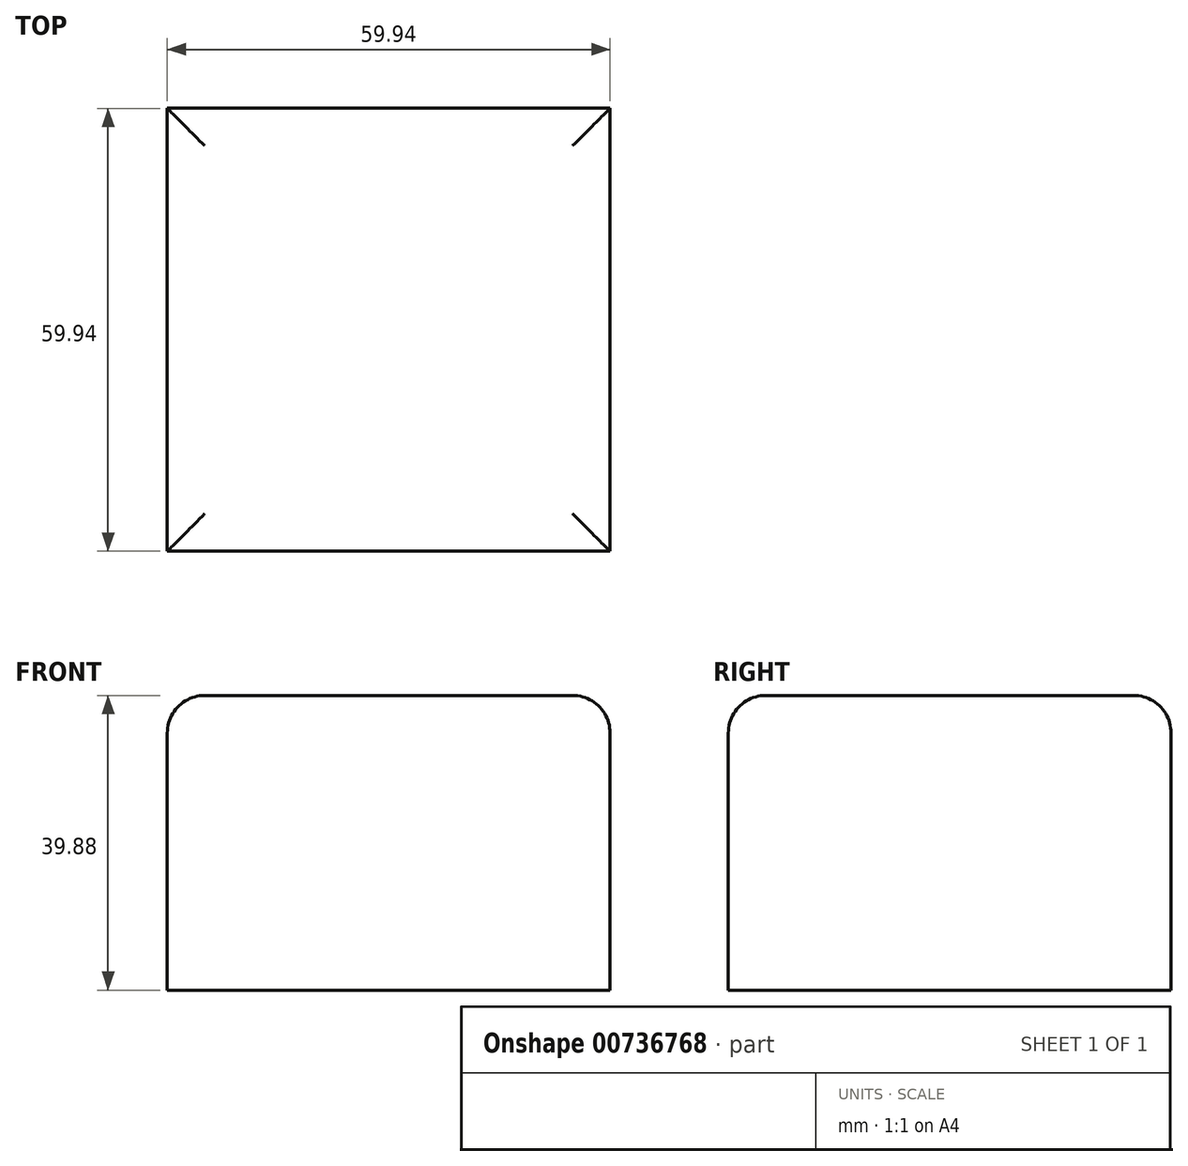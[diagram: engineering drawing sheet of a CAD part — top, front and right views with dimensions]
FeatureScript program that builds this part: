
annotation { "Feature Type Name" : "Feature", "Feature Type Description" : "" }
export const myFeature = defineFeature(function(context is Context, id is Id, definition is map)
    precondition{}
    {
        {
            var Q0;
            Q0=qCreatedBy(makeId("Top.planeOp"),FACE);
            var sketch = newSketch(context, id + "F0", { "sketchPlane" : qUnion([Q0])});
            skLineSegment(sketch, "E0.bottom", {"start": v(-37.43, 19.34) * mm, "end": v(22.51, 19.34) * mm});
            skLineSegment(sketch, "E0.top", {"start": v(-37.43, -40.6) * mm, "end": v(22.51, -40.6) * mm});
            skLineSegment(sketch, "E0.left", {"start": v(-37.43, 19.34) * mm, "end": v(-37.43, -40.6) * mm});
            skLineSegment(sketch, "E0.right", {"start": v(22.51, 19.34) * mm, "end": v(22.51, -40.6) * mm});
            skSolve(sketch);
        }
        {
            var Q0;
            Q0=makeQuery(id+"F0.imprint","IMPRINT",FACE,{"disambiguationData":[TD([[makeQuery(id+"F0.imprint","IMPRINT",EDGE,{"derivedFrom":sQuery(id+"F0.wireOp",EDGE,"E0.bottom")}),-1.0]])]});
            extrude(context, id + "F1", {"entities" : qUnion([Q0]), "depth" : 39.88 * mm, "offsetDistance" : 25.4 * mm});
        }
        {
            var Q0;
            Q0=makeQuery(id+"F1.opExtrude","CAP_EDGE",EDGE,{"disambiguationData":[OSD([sQuery(id+"F0.wireOp",EDGE,"E0.bottom")])],"isStart":false});
            var Q1;
            Q1=makeQuery(id+"F1.opExtrude","CAP_EDGE",EDGE,{"disambiguationData":[OSD([sQuery(id+"F0.wireOp",EDGE,"E0.left")])],"isStart":false});
            var Q2;
            Q2=makeQuery(id+"F1.opExtrude","CAP_EDGE",EDGE,{"disambiguationData":[OSD([sQuery(id+"F0.wireOp",EDGE,"E0.right")])],"isStart":false});
            var Q3;
            Q3=makeQuery(id+"F1.opExtrude","CAP_EDGE",EDGE,{"disambiguationData":[OSD([sQuery(id+"F0.wireOp",EDGE,"E0.top")])],"isStart":false});
            fillet(context, id + "F2", {"entities" : qUnion([Q0, Q1, Q2, Q3]), "radius" : 5.08 * mm, "tangentPropagation" : true, "allowEdgeOverflow" : false});
        }
    });
